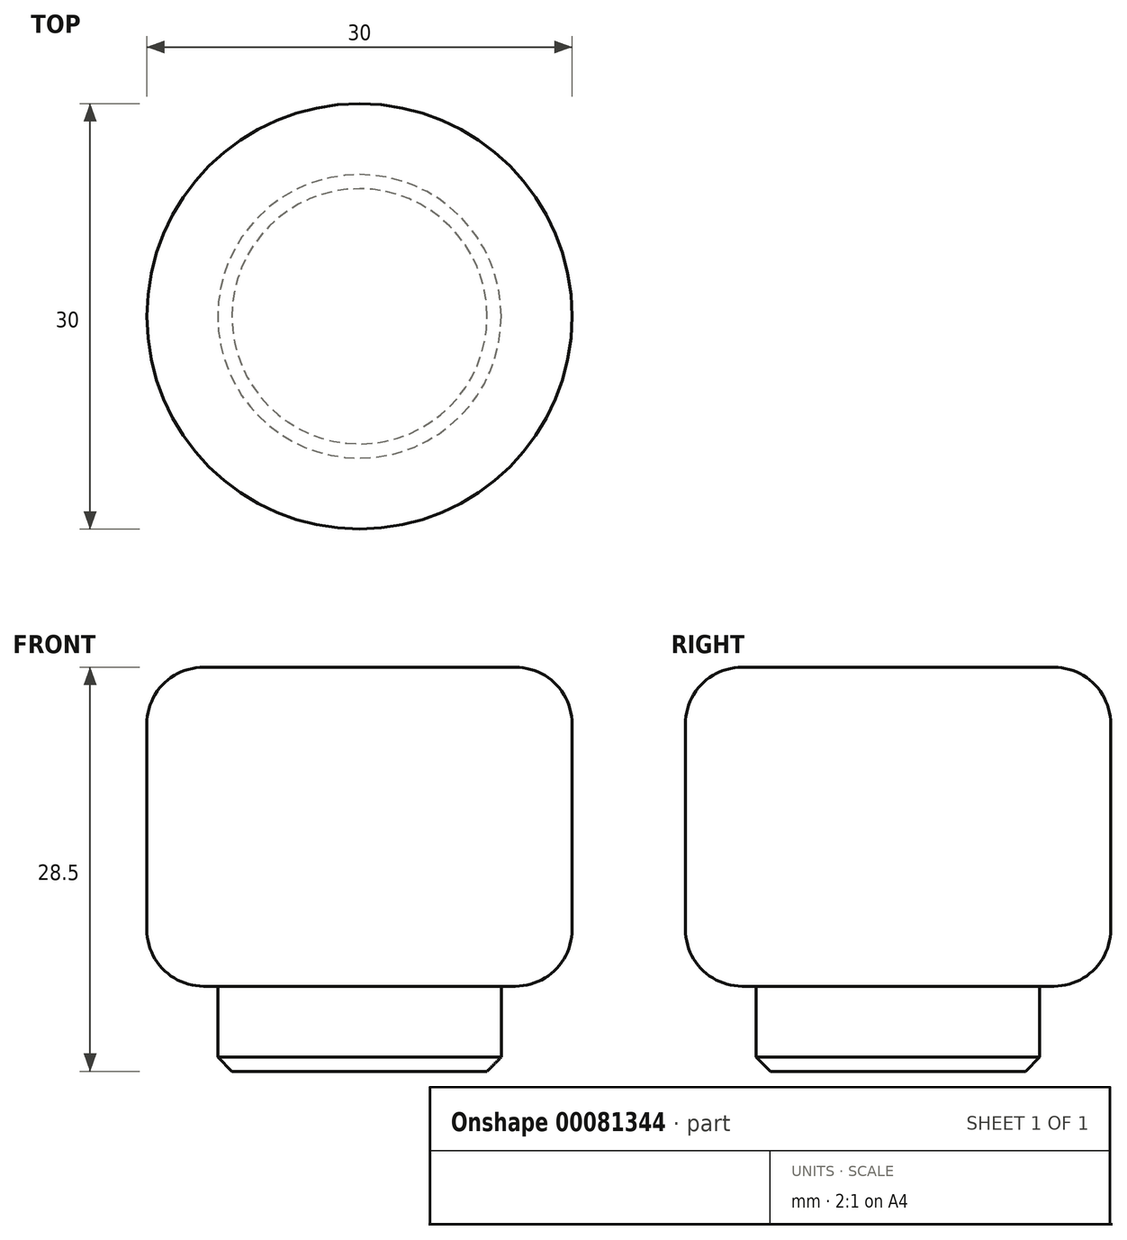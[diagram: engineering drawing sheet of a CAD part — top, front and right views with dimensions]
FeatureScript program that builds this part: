
annotation { "Feature Type Name" : "Feature", "Feature Type Description" : "" }
export const myFeature = defineFeature(function(context is Context, id is Id, definition is map)
    precondition{}
    {
        {
            var Q0;
            Q0=qCreatedBy(makeId("Front.planeOp"),FACE);
            var sketch = newSketch(context, id + "F0", { "sketchPlane" : qUnion([Q0])});
            skLineSegment(sketch, "E0", {"start": v(10, 1) * mm, "end": v(10, 6) * mm});
            skLineSegment(sketch, "E1", {"start": v(10, 6) * mm, "end": v(11, 6) * mm});
            skLineSegment(sketch, "E2", {"start": v(15, 10) * mm, "end": v(15, 24.5) * mm});
            skLineSegment(sketch, "E3", {"start": v(11, 28.5) * mm, "end": v(0, 28.5) * mm});
            skLineSegment(sketch, "E4", {"start": v(0, 28.5) * mm, "end": v(0, 0) * mm});
            skPoint(sketch, "E5.visualSharp", {"position": v(15, 28.5) * mm});
            skArc(sketch, "E5.filletArc", {"start": v(15, 24.5) * mm, "mid": v(13.83, 27.33) * mm, "end": v(11, 28.5) * mm});
            skPoint(sketch, "E6.visualSharp", {"position": v(15, 6) * mm});
            skArc(sketch, "E6.filletArc", {"start": v(11, 6) * mm, "mid": v(13.83, 7.17) * mm, "end": v(15, 10) * mm});
            skLineSegment(sketch, "E7", {"start": v(10, 1) * mm, "end": v(9, 0) * mm});
            skLineSegment(sketch, "E8", {"start": v(9, 0) * mm, "end": v(0, 0) * mm});
            skSolve(sketch);
        }
        {
            var Q0;
            Q0=makeQuery(id+"F0.imprint","IMPRINT",FACE,{"disambiguationData":[TD([[makeQuery(id+"F0.imprint","IMPRINT",EDGE,{"derivedFrom":sQuery(id+"F0.wireOp",EDGE,"E0")}),1.0]])]});
            var Q1;
            Q1=sQuery(id+"F0.wireOp",EDGE,"E4");
            revolve(context, id + "F1", {"surfaceOperationType" : NewSurfaceOperationType.NEW, "entities" : qUnion([Q0]), "axis" : qUnion([Q1]), "revolveType" : RevolveType.FULL});
        }
    });
